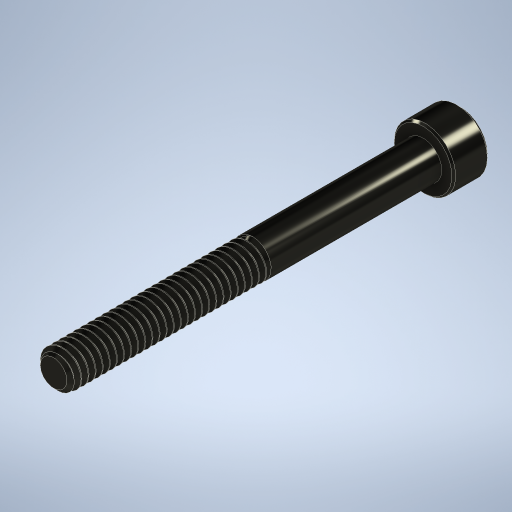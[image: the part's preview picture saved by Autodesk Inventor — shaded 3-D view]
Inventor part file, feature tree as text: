
AUTODESK INVENTOR PART (.ipt)
format: ipt  version: 2024 (Build 280153000, 153)  size: 836,096 bytes
history: native  units: in
note: dims shown in document units (in); Inventor stores cm internally (conversion verified against a paired STEP export)
features: chamfer x1
ambient origin geometry x8: Origin, YZ Plane, XZ Plane, XY Plane, X Axis, Y Axis, Z Axis, Center Point
bodies: Solid1 (feature_tree)
feature tree (1):
  chamfer  "Chamfer2"  [1 undecoded]
note: 1 required parameter value undecoded (feature->parameter linkage not recoverable at this tier; creation-order binding heuristic only, values carry confidence <= 0.55)
